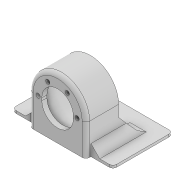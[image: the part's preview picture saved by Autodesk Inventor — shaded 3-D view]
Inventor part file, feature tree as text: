
AUTODESK INVENTOR PART (.ipt)
format: ipt  version: 2022 (Build 260153000, 153)  size: 208,896 bytes
history: native  units: mm
features: sketch x5, extrude x4, chamfer x3, fillet x2, hole x1, mirror x1
ambient origin geometry x8: Origin, YZ Plane, XZ Plane, XY Plane, X Axis, Y Axis, Z Axis, Center Point
bodies: Solid1 (feature_tree)
feature tree (16):
  extrude  "Extrusion1"  Depth=80.0mm
  extrude  "Extrusion2"  Depth=22.5mm
  extrude  "Extrusion3"  Depth=25.0mm
  hole  "Hole1"  [1 undecoded]
  extrude  "Extrusion4"  Depth=3.0mm
  mirror  "Mirror1"
  chamfer  "Chamfer1"  Distance=60.0mm Angle=360.0deg
  chamfer  "Chamfer2"  Distance=37.0mm
  chamfer  "Chamfer3"  Distance=6.5mm
  fillet  "Fillet1"  Radius=14.0mm
  fillet  "Fillet2"  Radius=12.0mm
  sketch  "Sketch1"  dims[d0=47.5mm d1=80.0mm]
  sketch  "Sketch2"  dims[d2=2.0mm d3=0.0mm d5=22.5mm]
  sketch  "Sketch3"  dims[d6=2.0mm d7=25.0mm]
  sketch  "Sketch4"  dims[d9=4.0mm d10=0.0mm d11=38.0mm]
  sketch  "Sketch5"  dims[d12=22.0mm d13=0.0mm d14=31.0mm d15=60.0mm d17=360.0deg d19=3.4mm d20=6.0mm d21=4.0mm d22=2.0mm d23=90.0deg d24=8.0mm d25=20.594885mm d27=37.0mm d28=6.5mm d29=14.0mm d30=12.0mm d31=3.0mm d32=0.0mm d33=0.5mm d34=2.0mm d35=45.0deg d36=3.0mm d37=2.0mm d38=45.0deg d39=7.0mm d40=2.0mm d41=45.0deg d42=3.0mm d43=3.0mm]
note: 1 required parameter value undecoded (feature->parameter linkage not recoverable at this tier; creation-order binding heuristic only, values carry confidence <= 0.55)
